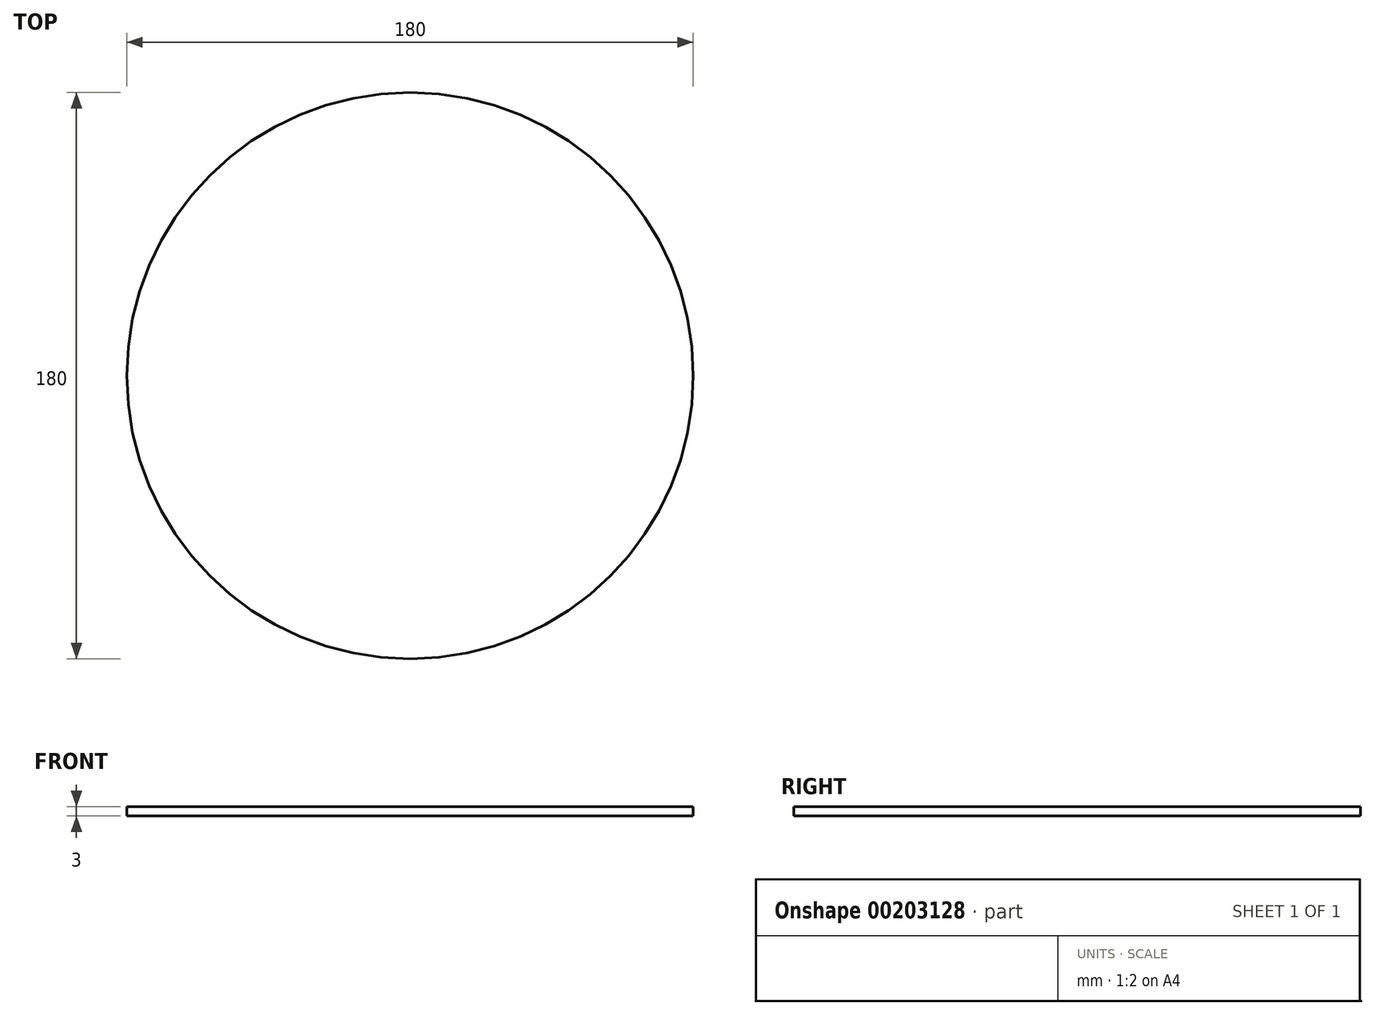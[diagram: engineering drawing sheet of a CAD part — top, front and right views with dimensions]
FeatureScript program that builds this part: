
annotation { "Feature Type Name" : "Feature", "Feature Type Description" : "" }
export const myFeature = defineFeature(function(context is Context, id is Id, definition is map)
    precondition{}
    {
        {
            var Q0;
            Q0=qCreatedBy(makeId("Top.planeOp"),FACE);
            var sketch = newSketch(context, id + "F0", { "sketchPlane" : qUnion([Q0])});
            skCircle(sketch, "E0", {"center": v(0, 0) * mm, "radius": 90 * mm});
            skSolve(sketch);
        }
        {
            var Q0;
            Q0 = qSketchRegion(id + "F0", true);
            extrude(context, id + "F1", {"entities" : qUnion([Q0]), "oppositeDirection" : true, "depth" : 3 * mm});
        }
    });
